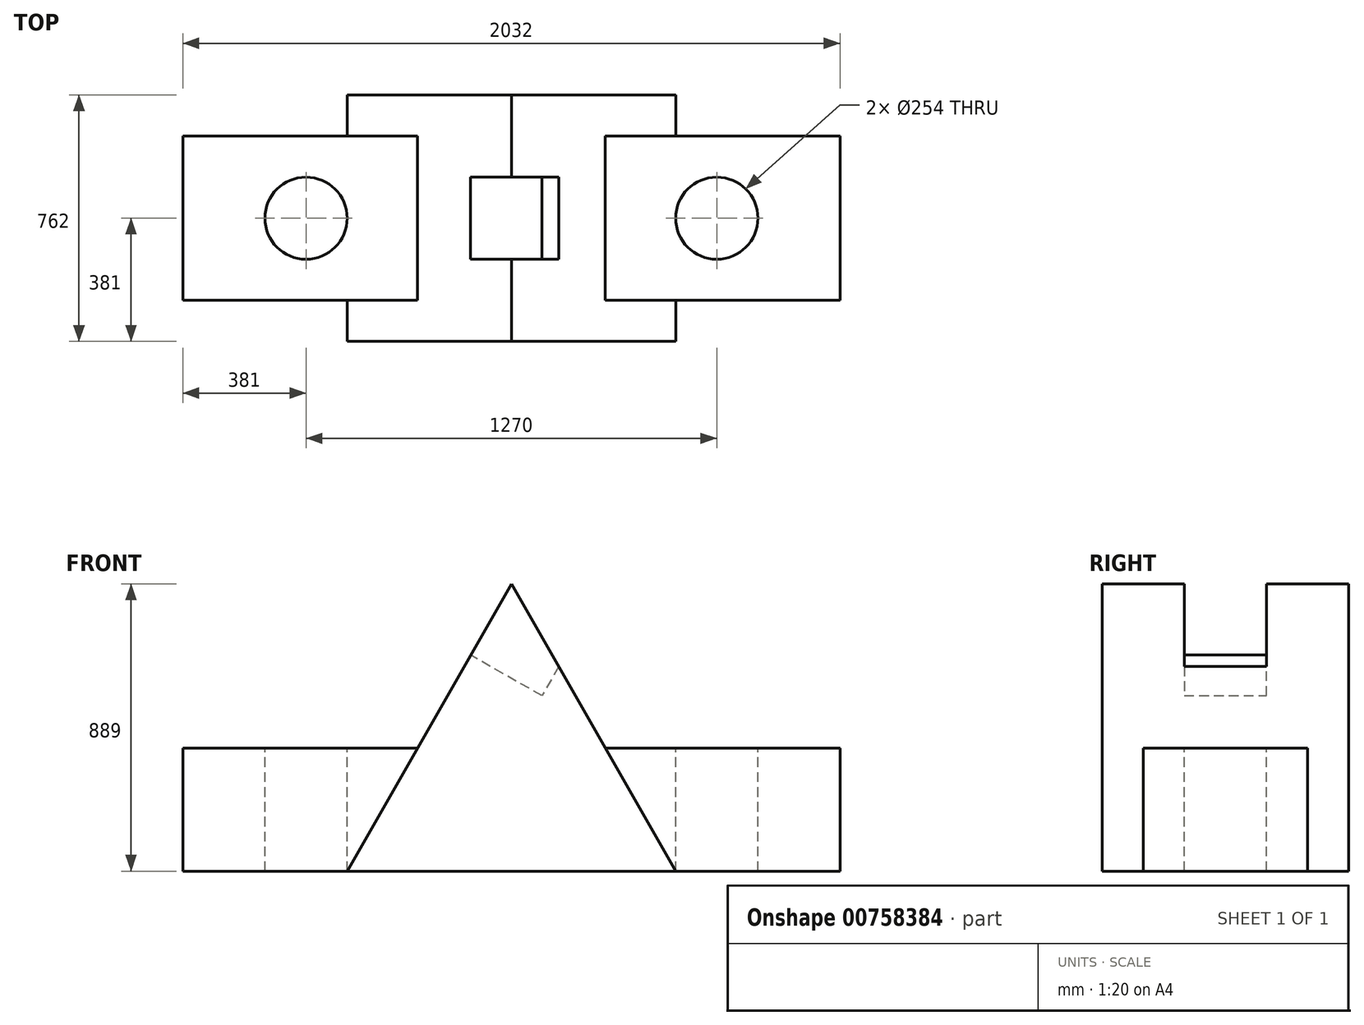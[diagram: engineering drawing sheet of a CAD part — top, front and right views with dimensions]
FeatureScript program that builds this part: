
annotation { "Feature Type Name" : "Feature", "Feature Type Description" : "" }
export const myFeature = defineFeature(function(context is Context, id is Id, definition is map)
    precondition{}
    {
        {
            var Q0;
            Q0=qCreatedBy(makeId("Front.planeOp"),FACE);
            var sketch = newSketch(context, id + "F0", { "sketchPlane" : qUnion([Q0])});
            skLineSegment(sketch, "E0.bottom", {"start": v(0, 0) * mm, "end": v(-2032, 0) * mm});
            skLineSegment(sketch, "E0.top", {"start": v(0, 889) * mm, "end": v(-2032, 889) * mm});
            skLineSegment(sketch, "E0.left", {"start": v(0, 0) * mm, "end": v(0, 889) * mm});
            skLineSegment(sketch, "E0.right", {"start": v(-2032, 0) * mm, "end": v(-2032, 889) * mm});
            skSolve(sketch);
        }
        {
            var Q0;
            Q0=makeQuery(id+"F0.imprint","IMPRINT",FACE,{"disambiguationData":[TD([[makeQuery(id+"F0.imprint","IMPRINT",EDGE,{"derivedFrom":sQuery(id+"F0.wireOp",EDGE,"E0.bottom")}),-1.0]])]});
            extrude(context, id + "F1", {"entities" : qUnion([Q0]), "depth" : 762 * mm, "offsetDistance" : 25.4 * mm});
        }
        {
            var Q0;
            Q0=makeQuery(id+"F1.opExtrude","CAP_FACE",FACE,{"disambiguationData":[OSD([sQuery(id+"F0.wireOp",EDGE,"E0.bottom"),sQuery(id+"F0.wireOp",EDGE,"E0.top"),sQuery(id+"F0.wireOp",EDGE,"E0.left"),sQuery(id+"F0.wireOp",EDGE,"E0.right")])],"isStart":false});
            var sketch = newSketch(context, id + "F2", { "sketchPlane" : qUnion([Q0])});
            skLineSegment(sketch, "E1", {"start": v(-2032, 0) * mm, "end": v(-1524, 0) * mm});
            skLineSegment(sketch, "E2", {"start": v(0, 0) * mm, "end": v(-508, 0) * mm});
            skLineSegment(sketch, "E3", {"start": v(-1524, 0) * mm, "end": v(-1016, 0) * mm});
            skLineSegment(sketch, "E4.bottom", {"start": v(-1016, 0) * mm, "end": v(-1016, 0) * mm});
            skLineSegment(sketch, "E4.top", {"start": v(-1016, 889) * mm, "end": v(-1016, 889) * mm});
            skLineSegment(sketch, "E4.left", {"start": v(-1016, 0) * mm, "end": v(-1016, 889) * mm});
            skLineSegment(sketch, "E4.right", {"start": v(-1016, 0) * mm, "end": v(-1016, 889) * mm});
            skLineSegment(sketch, "E5", {"start": v(-1524, 0) * mm, "end": v(-1016, 889) * mm});
            skLineSegment(sketch, "E6", {"start": v(-508, 0) * mm, "end": v(-1016, 889) * mm});
            skLineSegment(sketch, "E7", {"start": v(-2032, 0) * mm, "end": v(-2032, 889) * mm});
            skLineSegment(sketch, "E8", {"start": v(-2032, 889) * mm, "end": v(0, 889) * mm});
            skLineSegment(sketch, "E9", {"start": v(0, 889) * mm, "end": v(0, 0) * mm});
            skLineSegment(sketch, "E10", {"start": v(0, 0) * mm, "end": v(0, 381) * mm});
            skLineSegment(sketch, "E11", {"start": v(-2032, 0) * mm, "end": v(-2032, 381) * mm});
            skLineSegment(sketch, "E12", {"start": v(-2032, 381) * mm, "end": v(-1306.29, 381) * mm});
            skLineSegment(sketch, "E13", {"start": v(0, 381) * mm, "end": v(-725.71, 381) * mm});
            skSolve(sketch);
        }
        {
            var Q0;
            {var subQ0=sQuery(id+"F2.wireOp",EDGE,"E2");Q0=makeQuery(id+"F2.imprint","IMPRINT",FACE,{"disambiguationData":[TD([[makeQuery(id+"F2.imprint","IMPRINT",EDGE,{"derivedFrom":subQ0}),-1.0]])]});}
            var Q1;
            {var subQ0=sQuery(id+"F2.wireOp",EDGE,"E1");Q1=makeQuery(id+"F2.imprint","IMPRINT",FACE,{"disambiguationData":[TD([[makeQuery(id+"F2.imprint","IMPRINT",EDGE,{"derivedFrom":subQ0}),-1.0]])]});}
            extrude(context, id + "F3", {"entities" : qUnion([Q0, Q1]), "operationType" : NewBodyOperationType.REMOVE, "oppositeDirection" : true, "depth" : 127 * mm, "offsetDistance" : 25.4 * mm});
        }
        {
            var Q0;
            Q0=makeQuery(id+"F1.opExtrude","CAP_FACE",FACE,{"disambiguationData":[OSD([sQuery(id+"F0.wireOp",EDGE,"E0.bottom"),sQuery(id+"F0.wireOp",EDGE,"E0.top"),sQuery(id+"F0.wireOp",EDGE,"E0.left"),sQuery(id+"F0.wireOp",EDGE,"E0.right")])],"isStart":false});
            var sketch = newSketch(context, id + "F4", { "sketchPlane" : qUnion([Q0])});
            skLineSegment(sketch, "E14", {"start": v(-1306.29, 381) * mm, "end": v(-1016, 889) * mm});
            skLineSegment(sketch, "E15", {"start": v(-725.71, 381) * mm, "end": v(-1016, 889) * mm});
            skLineSegment(sketch, "E16", {"start": v(-1306.29, 381) * mm, "end": v(-2032, 381) * mm});
            skLineSegment(sketch, "E17", {"start": v(-2032, 381) * mm, "end": v(-2032, 889) * mm});
            skLineSegment(sketch, "E18", {"start": v(-2032, 889) * mm, "end": v(0, 889) * mm});
            skLineSegment(sketch, "E19", {"start": v(0, 889) * mm, "end": v(0, 381) * mm});
            skLineSegment(sketch, "E20", {"start": v(0, 381) * mm, "end": v(-725.71, 381) * mm});
            skSolve(sketch);
        }
        {
            var Q0;
            {var subQ0=sQuery(id+"F4.wireOp",EDGE,"E14");Q0=makeQuery(id+"F4.imprint","IMPRINT",FACE,{"disambiguationData":[TD([[makeQuery(id+"F4.imprint","IMPRINT",EDGE,{"derivedFrom":subQ0}),1.0]])]});}
            var Q1;
            {var subQ0=sQuery(id+"F4.wireOp",EDGE,"E15");Q1=makeQuery(id+"F4.imprint","IMPRINT",FACE,{"disambiguationData":[TD([[makeQuery(id+"F4.imprint","IMPRINT",EDGE,{"derivedFrom":subQ0}),-1.0]])]});}
            extrude(context, id + "F5", {"entities" : qUnion([Q0, Q1]), "operationType" : NewBodyOperationType.ADD, "oppositeDirection" : true, "depth" : 762 * mm, "offsetDistance" : 25.4 * mm});
        }
        {
            var Q0;
            Q0=makeQuery(id+"F1.opExtrude","CAP_FACE",FACE,{"disambiguationData":[OSD([sQuery(id+"F0.wireOp",EDGE,"E0.bottom"),sQuery(id+"F0.wireOp",EDGE,"E0.top"),sQuery(id+"F0.wireOp",EDGE,"E0.left"),sQuery(id+"F0.wireOp",EDGE,"E0.right")])],"isStart":false});
            var sketch = newSketch(context, id + "F6", { "sketchPlane" : qUnion([Q0])});
            skLineSegment(sketch, "E21", {"start": v(-1306.29, 381) * mm, "end": v(-1016, 889) * mm});
            skLineSegment(sketch, "E22", {"start": v(-725.71, 381) * mm, "end": v(-1016, 889) * mm});
            skLineSegment(sketch, "E23", {"start": v(-1016, 889) * mm, "end": v(-2032, 889) * mm});
            skLineSegment(sketch, "E24", {"start": v(-2032, 889) * mm, "end": v(-2032, 381) * mm});
            skLineSegment(sketch, "E25", {"start": v(-2032, 381) * mm, "end": v(-1306.29, 381) * mm});
            skSolve(sketch);
        }
        {
            var Q0;
            Q0=makeQuery(id+"F6.imprint","IMPRINT",FACE,{"disambiguationData":[TD([[makeQuery(id+"F6.imprint","IMPRINT",EDGE,{"derivedFrom":sQuery(id+"F6.wireOp",EDGE,"E21")}),1.0]])]});
            extrude(context, id + "F7", {"entities" : qUnion([Q0]), "operationType" : NewBodyOperationType.REMOVE, "oppositeDirection" : true, "depth" : 889 * mm, "offsetDistance" : 25.4 * mm});
        }
        {
            var Q0;
            Q0=makeQuery(id+"F1.opExtrude","CAP_FACE",FACE,{"disambiguationData":[OSD([sQuery(id+"F0.wireOp",EDGE,"E0.bottom"),sQuery(id+"F0.wireOp",EDGE,"E0.top"),sQuery(id+"F0.wireOp",EDGE,"E0.left"),sQuery(id+"F0.wireOp",EDGE,"E0.right")])],"isStart":false});
            var sketch = newSketch(context, id + "F8", { "sketchPlane" : qUnion([Q0])});
            skLineSegment(sketch, "E26", {"start": v(-725.71, 381) * mm, "end": v(-1016, 889) * mm});
            skLineSegment(sketch, "E27", {"start": v(0, 889) * mm, "end": v(-1016, 889) * mm});
            skLineSegment(sketch, "E28", {"start": v(0, 381) * mm, "end": v(-725.71, 381) * mm});
            skLineSegment(sketch, "E29", {"start": v(0, 381) * mm, "end": v(0, 889) * mm});
            skSolve(sketch);
        }
        {
            var Q0;
            Q0=makeQuery(id+"F8.imprint","IMPRINT",FACE,{"disambiguationData":[TD([[makeQuery(id+"F8.imprint","IMPRINT",EDGE,{"derivedFrom":sQuery(id+"F8.wireOp",EDGE,"E26")}),-1.0]])]});
            extrude(context, id + "F9", {"entities" : qUnion([Q0]), "operationType" : NewBodyOperationType.REMOVE, "oppositeDirection" : true, "depth" : 762 * mm, "offsetDistance" : 25.4 * mm});
        }
        {
            var Q0;
            Q0=makeQuery(id+"F1.opExtrude","CAP_FACE",FACE,{"disambiguationData":[OSD([sQuery(id+"F0.wireOp",EDGE,"E0.bottom"),sQuery(id+"F0.wireOp",EDGE,"E0.top"),sQuery(id+"F0.wireOp",EDGE,"E0.left"),sQuery(id+"F0.wireOp",EDGE,"E0.right")])],"isStart":true});
            var sketch = newSketch(context, id + "F10", { "sketchPlane" : qUnion([Q0])});
            skLineSegment(sketch, "E30", {"start": v(0, 0) * mm, "end": v(508, 0) * mm});
            skLineSegment(sketch, "E31", {"start": v(508, 0) * mm, "end": v(725.71, 381) * mm});
            skLineSegment(sketch, "E32", {"start": v(725.71, 381) * mm, "end": v(0, 381) * mm});
            skLineSegment(sketch, "E33", {"start": v(0, 381) * mm, "end": v(0, 0) * mm});
            skLineSegment(sketch, "E34", {"start": v(1306.29, 381) * mm, "end": v(2032, 381) * mm});
            skLineSegment(sketch, "E35", {"start": v(2032, 381) * mm, "end": v(2032, 0) * mm});
            skLineSegment(sketch, "E36", {"start": v(2032, 0) * mm, "end": v(1524, 0) * mm});
            skLineSegment(sketch, "E37", {"start": v(1524, 0) * mm, "end": v(1306.29, 381) * mm});
            skSolve(sketch);
        }
        {
            var Q0;
            Q0=makeQuery(id+"F10.imprint","IMPRINT",FACE,{"disambiguationData":[TD([[makeQuery(id+"F10.imprint","IMPRINT",EDGE,{"derivedFrom":sQuery(id+"F10.wireOp",EDGE,"E30")}),1.0]])]});
            var Q1;
            Q1=makeQuery(id+"F10.imprint","IMPRINT",FACE,{"disambiguationData":[TD([[makeQuery(id+"F10.imprint","IMPRINT",EDGE,{"derivedFrom":sQuery(id+"F10.wireOp",EDGE,"E34")}),1.0]])]});
            extrude(context, id + "F11", {"entities" : qUnion([Q0, Q1]), "operationType" : NewBodyOperationType.REMOVE, "oppositeDirection" : true, "depth" : 127 * mm, "offsetDistance" : 25.4 * mm});
        }
        {
            var Q0;
            Q0=makeQuery(id+"F11.boolean.opBoolean","MERGE",FACE,{"derivedFrom":[makeQuery(id+"F9.boolean.opBoolean","MERGE",FACE,{"derivedFrom":[makeQuery(id+"F3.boolean.opBoolean","COPY",FACE,{"derivedFrom":makeQuery(id+"F3.opExtrude","SWEPT_FACE",FACE,{"disambiguationData":[OSD([sQuery(id+"F2.wireOp",EDGE,"E6")])]})}),makeQuery(id+"F9.opExtrude","SWEPT_FACE",FACE,{"disambiguationData":[OSD([sQuery(id+"F8.wireOp",EDGE,"E26")])]})]}),makeQuery(id+"F11.opExtrude","SWEPT_FACE",FACE,{"disambiguationData":[OSD([sQuery(id+"F10.wireOp",EDGE,"E31")])]})]});
            var sketch = newSketch(context, id + "F12", { "sketchPlane" : qUnion([Q0])});
            skLineSegment(sketch, "E38", {"start": v(-762, 1275.95) * mm, "end": v(-762, 1021.95) * mm});
            skLineSegment(sketch, "E39", {"start": v(-762, 1275.95) * mm, "end": v(-508, 1275.95) * mm});
            skLineSegment(sketch, "E40", {"start": v(0, 1275.95) * mm, "end": v(-254, 1275.95) * mm});
            skLineSegment(sketch, "E41", {"start": v(0, 1275.95) * mm, "end": v(0, 1021.95) * mm});
            skLineSegment(sketch, "E42", {"start": v(-762, 1021.95) * mm, "end": v(0, 1021.95) * mm});
            skLineSegment(sketch, "E43", {"start": v(-508, 1275.95) * mm, "end": v(-508, 1021.95) * mm});
            skLineSegment(sketch, "E44", {"start": v(-254, 1275.95) * mm, "end": v(-254, 1021.95) * mm});
            skLineSegment(sketch, "E45", {"start": v(-254, 1275.95) * mm, "end": v(-508, 1275.95) * mm});
            skLineSegment(sketch, "E46", {"start": v(-508, 1021.95) * mm, "end": v(-254, 1021.95) * mm});
            skSolve(sketch);
        }
        {
            var Q0;
            Q0=makeQuery(id+"F12.imprint","IMPRINT",FACE,{"disambiguationData":[TD([[makeQuery(id+"F12.imprint","IMPRINT",EDGE,{"derivedFrom":sQuery(id+"F12.wireOp",EDGE,"E43")}),1.0]])]});
            extrude(context, id + "F13", {"entities" : qUnion([Q0]), "operationType" : NewBodyOperationType.REMOVE, "depth" : 254 * mm, "offsetDistance" : 25.4 * mm});
        }
        {
            var Q0;
            Q0=makeQuery(id+"F7.boolean.opBoolean","COPY",FACE,{"derivedFrom":makeQuery(id+"F7.opExtrude","SWEPT_FACE",FACE,{"disambiguationData":[OSD([sQuery(id+"F6.wireOp",EDGE,"E25")])]})});
            var sketch = newSketch(context, id + "F14", { "sketchPlane" : qUnion([Q0])});
            skLineSegment(sketch, "E47", {"start": v(-2032, -127) * mm, "end": v(-1651, -127) * mm});
            skLineSegment(sketch, "E48", {"start": v(-2032, -127) * mm, "end": v(-2032, -381) * mm});
            skLineSegment(sketch, "E49", {"start": v(-1651, -127) * mm, "end": v(-1651, -381) * mm});
            skLineSegment(sketch, "E50", {"start": v(-2032, -381) * mm, "end": v(-1651, -381) * mm});
            skCircle(sketch, "E51", {"center": v(-1651, -381) * mm, "radius": 127 * mm});
            skSolve(sketch);
        }
        {
            var Q0;
            {var subQ0=sQuery(id+"F14.wireOp",EDGE,"E50");var subQ1=sQuery(id+"F14.wireOp",EDGE,"E49");var subQ2=makeQuery(id+"F14.imprint","INTERSECT",VERTEX,{"derivedFrom":[subQ1,subQ0]});Q0=makeQuery(id+"F14.imprint","IMPRINT",FACE,{"disambiguationData":[TD([[makeQuery(id+"F14.imprint","IMPRINT",EDGE,{"disambiguationData":[TD([[subQ2,1.0]])],"derivedFrom":subQ1}),1.0]])]});}
            var Q1;
            {var subQ0=sQuery(id+"F14.wireOp",EDGE,"E50");var subQ1=sQuery(id+"F14.wireOp",EDGE,"E49");var subQ2=makeQuery(id+"F14.imprint","INTERSECT",VERTEX,{"derivedFrom":[subQ1,subQ0]});Q1=makeQuery(id+"F14.imprint","IMPRINT",FACE,{"disambiguationData":[TD([[makeQuery(id+"F14.imprint","IMPRINT",EDGE,{"disambiguationData":[TD([[subQ2,1.0]])],"derivedFrom":subQ1}),-1.0]])]});}
            extrude(context, id + "F15", {"entities" : qUnion([Q0, Q1]), "operationType" : NewBodyOperationType.REMOVE, "oppositeDirection" : true, "depth" : 381 * mm, "offsetDistance" : 25.4 * mm});
        }
        {
            var Q0;
            Q0=makeQuery(id+"F9.boolean.opBoolean","COPY",FACE,{"derivedFrom":makeQuery(id+"F9.opExtrude","SWEPT_FACE",FACE,{"disambiguationData":[OSD([sQuery(id+"F8.wireOp",EDGE,"E28")])]})});
            var sketch = newSketch(context, id + "F16", { "sketchPlane" : qUnion([Q0])});
            skLineSegment(sketch, "E52", {"start": v(0, -127) * mm, "end": v(-381, -127) * mm});
            skLineSegment(sketch, "E53", {"start": v(0, -127) * mm, "end": v(0, -381) * mm});
            skLineSegment(sketch, "E54", {"start": v(0, -381) * mm, "end": v(-381, -381) * mm});
            skLineSegment(sketch, "E55", {"start": v(-381, -381) * mm, "end": v(-381, -127) * mm});
            skCircle(sketch, "E56", {"center": v(-381, -381) * mm, "radius": 127 * mm});
            skSolve(sketch);
        }
        {
            var Q0;
            {var subQ0=sQuery(id+"F16.wireOp",EDGE,"E55");var subQ1=sQuery(id+"F16.wireOp",EDGE,"E54");var subQ2=makeQuery(id+"F16.imprint","INTERSECT",VERTEX,{"derivedFrom":[subQ1,subQ0]});Q0=makeQuery(id+"F16.imprint","IMPRINT",FACE,{"disambiguationData":[TD([[makeQuery(id+"F16.imprint","IMPRINT",EDGE,{"disambiguationData":[TD([[subQ2,1.0]])],"derivedFrom":subQ1}),-1.0]])]});}
            var Q1;
            {var subQ0=sQuery(id+"F16.wireOp",EDGE,"E55");var subQ1=sQuery(id+"F16.wireOp",EDGE,"E54");var subQ2=makeQuery(id+"F16.imprint","INTERSECT",VERTEX,{"derivedFrom":[subQ1,subQ0]});Q1=makeQuery(id+"F16.imprint","IMPRINT",FACE,{"disambiguationData":[TD([[makeQuery(id+"F16.imprint","IMPRINT",EDGE,{"disambiguationData":[TD([[subQ2,1.0]])],"derivedFrom":subQ1}),1.0]])]});}
            extrude(context, id + "F17", {"entities" : qUnion([Q0, Q1]), "operationType" : NewBodyOperationType.ADD, "oppositeDirection" : true, "depth" : 381 * mm, "offsetDistance" : 25.4 * mm});
        }
        {
            var Q0;
            Q0=makeQuery(id+"F9.boolean.opBoolean","COPY",FACE,{"derivedFrom":makeQuery(id+"F9.opExtrude","SWEPT_FACE",FACE,{"disambiguationData":[OSD([sQuery(id+"F8.wireOp",EDGE,"E28")])]})});
            var sketch = newSketch(context, id + "F18", { "sketchPlane" : qUnion([Q0])});
            skLineSegment(sketch, "E57", {"start": v(0, -127) * mm, "end": v(-381, -127) * mm});
            skLineSegment(sketch, "E58", {"start": v(0, -127) * mm, "end": v(0, -381) * mm});
            skLineSegment(sketch, "E59", {"start": v(0, -381) * mm, "end": v(-381, -381) * mm});
            skCircle(sketch, "E60", {"center": v(-381, -381) * mm, "radius": 127 * mm});
            skSolve(sketch);
        }
        {
            var Q0;
            Q0 = qSketchRegion(id + "F18", true);
            extrude(context, id + "F19", {"entities" : qUnion([Q0]), "operationType" : NewBodyOperationType.ADD, "oppositeDirection" : true, "depth" : 381 * mm, "offsetDistance" : 25.4 * mm});
        }
        {
            var Q0;
            Q0=makeQuery(id+"F9.boolean.opBoolean","COPY",FACE,{"derivedFrom":makeQuery(id+"F9.opExtrude","SWEPT_FACE",FACE,{"disambiguationData":[OSD([sQuery(id+"F8.wireOp",EDGE,"E28")])]})});
            var sketch = newSketch(context, id + "F20", { "sketchPlane" : qUnion([Q0])});
            skLineSegment(sketch, "E61", {"start": v(0, -127) * mm, "end": v(-381, -127) * mm});
            skLineSegment(sketch, "E62", {"start": v(0, -127) * mm, "end": v(0, -381) * mm});
            skLineSegment(sketch, "E63", {"start": v(0, -381) * mm, "end": v(-381, -381) * mm});
            skCircle(sketch, "E64", {"center": v(-381, -381) * mm, "radius": 127 * mm});
            skSolve(sketch);
        }
        {
            var Q0;
            Q0 = qSketchRegion(id + "F20", true);
            extrude(context, id + "F21", {"entities" : qUnion([Q0]), "operationType" : NewBodyOperationType.REMOVE, "depth" : 381 * mm, "offsetDistance" : 25.4 * mm});
        }
        {
            var Q0;
            Q0=makeQuery(id+"F9.boolean.opBoolean","COPY",FACE,{"derivedFrom":makeQuery(id+"F9.opExtrude","SWEPT_FACE",FACE,{"disambiguationData":[OSD([sQuery(id+"F8.wireOp",EDGE,"E28")])]})});
            var sketch = newSketch(context, id + "F22", { "sketchPlane" : qUnion([Q0])});
            skLineSegment(sketch, "E65", {"start": v(0, -127) * mm, "end": v(-381, -127) * mm});
            skLineSegment(sketch, "E66", {"start": v(0, -127) * mm, "end": v(0, -381) * mm});
            skLineSegment(sketch, "E67", {"start": v(0, -381) * mm, "end": v(-381, -381) * mm});
            skCircle(sketch, "E68", {"center": v(-381, -381) * mm, "radius": 127 * mm});
            skSolve(sketch);
        }
        {
            var Q0;
            Q0=makeQuery(id+"F22.imprint","IMPRINT",FACE,{"disambiguationData":[TD([[makeQuery(id+"F22.imprint","IMPRINT",EDGE,{"derivedFrom":sQuery(id+"F22.wireOp",EDGE,"E68")}),1.0]])]});
            extrude(context, id + "F23", {"entities" : qUnion([Q0]), "operationType" : NewBodyOperationType.REMOVE, "oppositeDirection" : true, "depth" : 381 * mm, "offsetDistance" : 25.4 * mm});
        }
        {
            var Q0;
            Q0=makeQuery(id+"F11.boolean.opBoolean","MERGE",FACE,{"derivedFrom":[makeQuery(id+"F7.boolean.opBoolean","MERGE",FACE,{"derivedFrom":[makeQuery(id+"F3.boolean.opBoolean","COPY",FACE,{"derivedFrom":makeQuery(id+"F3.opExtrude","SWEPT_FACE",FACE,{"disambiguationData":[OSD([sQuery(id+"F2.wireOp",EDGE,"E5")])]})}),makeQuery(id+"F7.opExtrude","SWEPT_FACE",FACE,{"disambiguationData":[OSD([sQuery(id+"F6.wireOp",EDGE,"E21")])]})]}),makeQuery(id+"F11.opExtrude","SWEPT_FACE",FACE,{"disambiguationData":[OSD([sQuery(id+"F10.wireOp",EDGE,"E37")])]})]});
            var sketch = newSketch(context, id + "F24", { "sketchPlane" : qUnion([Q0])});
            skLineSegment(sketch, "E69", {"start": v(0, 267.8) * mm, "end": v(254, 267.8) * mm});
            skLineSegment(sketch, "E70", {"start": v(762, 267.8) * mm, "end": v(508, 267.8) * mm});
            skLineSegment(sketch, "E71", {"start": v(508, 267.8) * mm, "end": v(508, 521.8) * mm});
            skLineSegment(sketch, "E72", {"start": v(508, 267.8) * mm, "end": v(508, 13.8) * mm});
            skLineSegment(sketch, "E73", {"start": v(508, 13.8) * mm, "end": v(254, 13.8) * mm});
            skLineSegment(sketch, "E74", {"start": v(254, 267.8) * mm, "end": v(254, 13.8) * mm});
            skLineSegment(sketch, "E75", {"start": v(508, 521.8) * mm, "end": v(254, 521.8) * mm});
            skLineSegment(sketch, "E76", {"start": v(254, 267.8) * mm, "end": v(254, 521.8) * mm});
            skSolve(sketch);
        }
        {
            var Q0;
            {var subQ0=sQuery(id+"F24.wireOp",EDGE,"E72");Q0=makeQuery(id+"F24.imprint","IMPRINT",FACE,{"disambiguationData":[TD([[makeQuery(id+"F24.imprint","IMPRINT",EDGE,{"derivedFrom":subQ0}),-1.0]])]});}
            var Q1;
            {var subQ0=sQuery(id+"F24.wireOp",EDGE,"E71");Q1=makeQuery(id+"F24.imprint","IMPRINT",FACE,{"disambiguationData":[TD([[makeQuery(id+"F24.imprint","IMPRINT",EDGE,{"derivedFrom":subQ0}),1.0]])]});}
            extrude(context, id + "F25", {"entities" : qUnion([Q0, Q1]), "operationType" : NewBodyOperationType.REMOVE, "oppositeDirection" : true, "depth" : 254 * mm, "offsetDistance" : 25.4 * mm});
        }
    });
